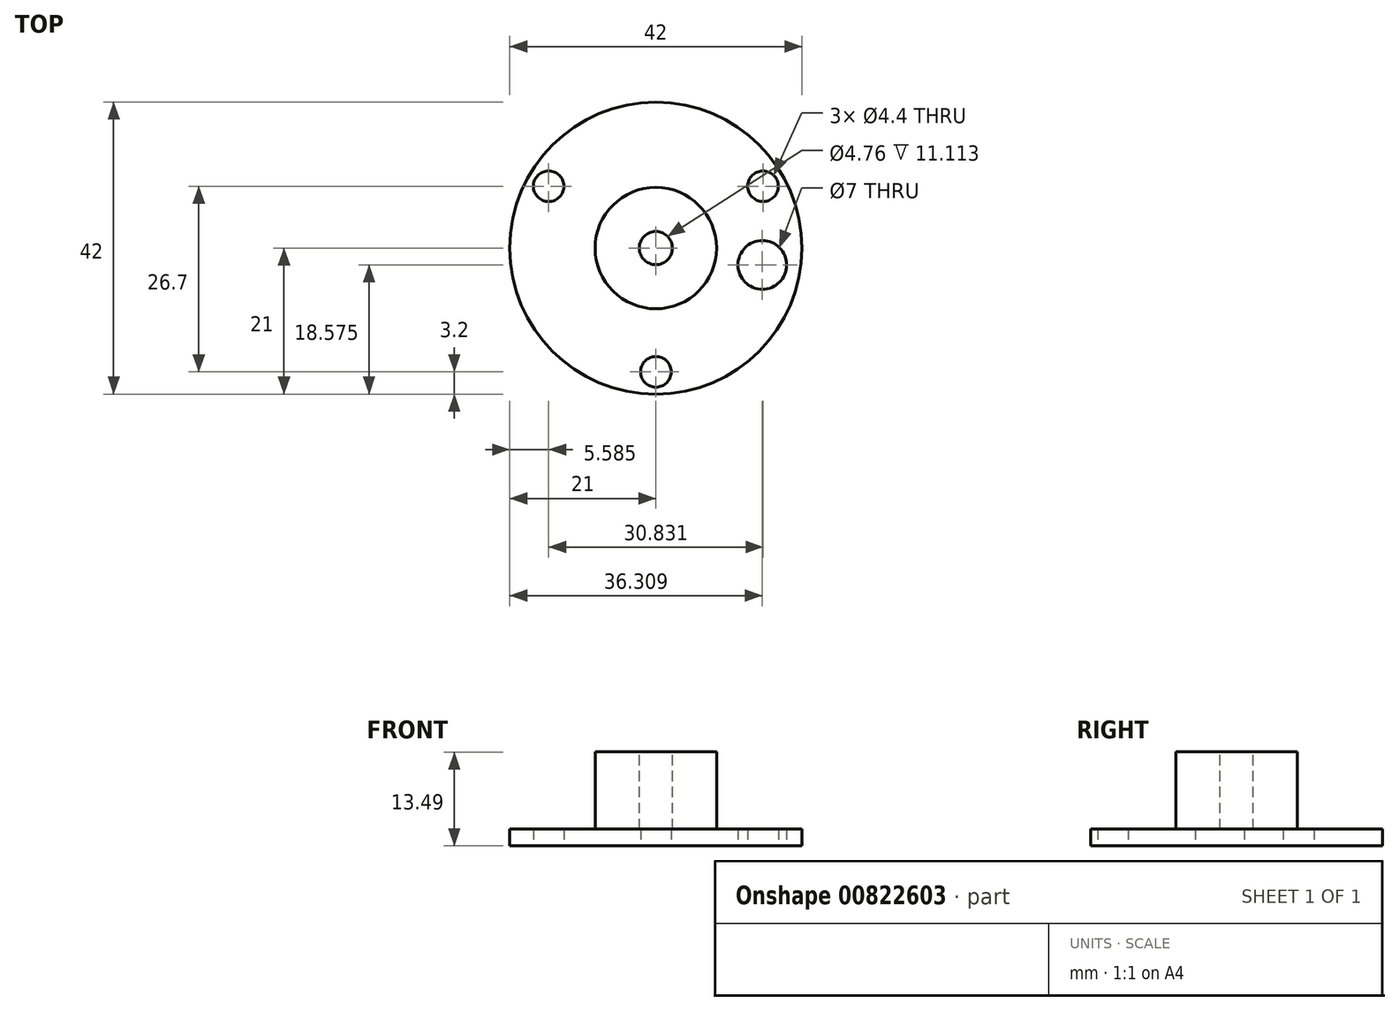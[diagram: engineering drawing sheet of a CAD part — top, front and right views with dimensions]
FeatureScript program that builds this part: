
annotation { "Feature Type Name" : "Feature", "Feature Type Description" : "" }
export const myFeature = defineFeature(function(context is Context, id is Id, definition is map)
    precondition{}
    {
        {
            var Q0;
            Q0=qCreatedBy(makeId("Top.planeOp"),FACE);
            var sketch = newSketch(context, id + "F0", { "sketchPlane" : qUnion([Q0])});
            skCircle(sketch, "E0", {"center": v(0, 0) * mm, "radius": 21 * mm});
            skSolve(sketch);
        }
        {
            var Q0;
            Q0=makeQuery(id+"F0.imprint","IMPRINT",FACE,{"disambiguationData":[TD([[makeQuery(id+"F0.imprint","IMPRINT",EDGE,{"derivedFrom":sQuery(id+"F0.wireOp",EDGE,"E0")}),1.0]])]});
            var sketch = newSketch(context, id + "F1", { "sketchPlane" : qUnion([Q0])});
            skCircle(sketch, "E1", {"center": v(0, 0) * mm, "radius": 8.73 * mm});
            skSolve(sketch);
        }
        {
            var Q0;
            Q0=makeQuery(id+"F0.imprint","IMPRINT",FACE,{"disambiguationData":[TD([[makeQuery(id+"F0.imprint","IMPRINT",EDGE,{"derivedFrom":sQuery(id+"F0.wireOp",EDGE,"E0")}),1.0]])]});
            extrude(context, id + "F2", {"entities" : qUnion([Q0]), "depth" : 2.38 * mm, "offsetDistance" : 25.4 * mm});
        }
        {
            var Q0;
            Q0=makeQuery(id+"F1.imprint","IMPRINT",FACE,{"disambiguationData":[TD([[makeQuery(id+"F1.imprint","IMPRINT",EDGE,{"derivedFrom":sQuery(id+"F1.wireOp",EDGE,"E1")}),1.0]])]});
            extrude(context, id + "F3", {"entities" : qUnion([Q0]), "operationType" : NewBodyOperationType.ADD, "depth" : 13.5 * mm, "offsetDistance" : 25.4 * mm});
        }
        {
            var Q0;
            Q0=makeQuery(id+"F3.opExtrude","CAP_FACE",FACE,{"disambiguationData":[OSD([sQuery(id+"F1.wireOp",EDGE,"E1")])],"isStart":false});
            var sketch = newSketch(context, id + "F4", { "sketchPlane" : qUnion([Q0])});
            skCircle(sketch, "E2", {"center": v(0, 0) * mm, "radius": 2.38 * mm});
            skSolve(sketch);
        }
        {
            var Q0;
            Q0 = qSketchRegion(id + "F4", true);
            extrude(context, id + "F5", {"entities" : qUnion([Q0]), "operationType" : NewBodyOperationType.REMOVE, "oppositeDirection" : true, "depth" : 11.1 * mm, "offsetDistance" : 25.4 * mm});
        }
        {
            var Q0;
            Q0=makeQuery(id+"F2.opExtrude","CAP_FACE",FACE,{"disambiguationData":[OSD([sQuery(id+"F0.wireOp",EDGE,"E0")])],"isStart":true});
            var sketch = newSketch(context, id + "F6", { "sketchPlane" : qUnion([Q0])});
            skCircle(sketch, "E3", {"center": v(0, 17.8) * mm, "radius": 2.2 * mm});
            skCircle(sketch, "E4", {"center": v(15.42, -8.9) * mm, "radius": 2.2 * mm});
            skCircle(sketch, "E5", {"center": v(-15.42, -8.9) * mm, "radius": 2.2 * mm});
            skCircle(sketch, "E6", {"center": v(15.3, 2.42) * mm, "radius": 3.5 * mm});
            skLineSegment(sketch, "E7", {"start": v(0, 17.8) * mm, "end": v(0, 0) * mm});
            skLineSegment(sketch, "E8", {"start": v(-15.42, -8.9) * mm, "end": v(0, 0) * mm});
            skLineSegment(sketch, "E9", {"start": v(15.3, 2.42) * mm, "end": v(0, 0) * mm});
            skLineSegment(sketch, "E10", {"start": v(15.42, -8.9) * mm, "end": v(0, 0) * mm});
            skSolve(sketch);
        }
        {
            var Q0;
            Q0=makeQuery(id+"F6.imprint","IMPRINT",FACE,{"disambiguationData":[TD([[makeQuery(id+"F6.imprint","IMPRINT",EDGE,{"derivedFrom":sQuery(id+"F6.wireOp",EDGE,"E3")}),1.0]])]});
            extrude(context, id + "F7", {"entities" : qUnion([Q0]), "operationType" : NewBodyOperationType.REMOVE, "oppositeDirection" : true, "depth" : 2.38 * mm, "offsetDistance" : 25.4 * mm});
        }
        {
            var Q0;
            Q0 = qSketchRegion(id + "F6", true);
            extrude(context, id + "F8", {"entities" : qUnion([Q0]), "operationType" : NewBodyOperationType.REMOVE, "oppositeDirection" : true, "depth" : 2.38 * mm, "offsetDistance" : 25.4 * mm});
        }
    });
